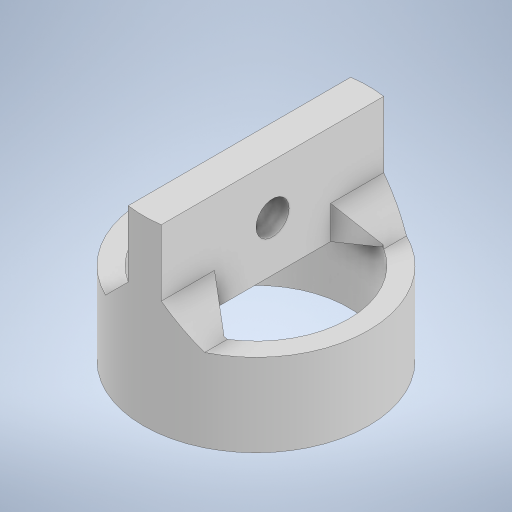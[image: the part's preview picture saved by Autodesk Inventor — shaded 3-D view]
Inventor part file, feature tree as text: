
AUTODESK INVENTOR PART (.ipt)
format: ipt  version: 2024 (Build 280153000, 153)  size: 268,288 bytes
history: native  units: mm
features: extrude x3, chamfer x2, other x1, sketch x1, projected_geometry x1
ambient origin geometry x8: Origin, YZ Plane, XZ Plane, XY Plane, X Axis, Y Axis, Z Axis, Center Point
bodies: Body1 (feature_tree)
feature tree (8):
  other  "솔리드1"
  extrude  "돌출1"  Depth=5.6mm
  extrude  "돌출2"  Depth=6.8mm
  chamfer  "모따기1"  Distance=2.5mm
  chamfer  "모따기2"  Distance=1.0mm
  extrude  "돌출4"  Depth=3.0mm TaperAngle=0.0deg
  sketch  "스케치5"
  projected_geometry  "투영된 루프3"
